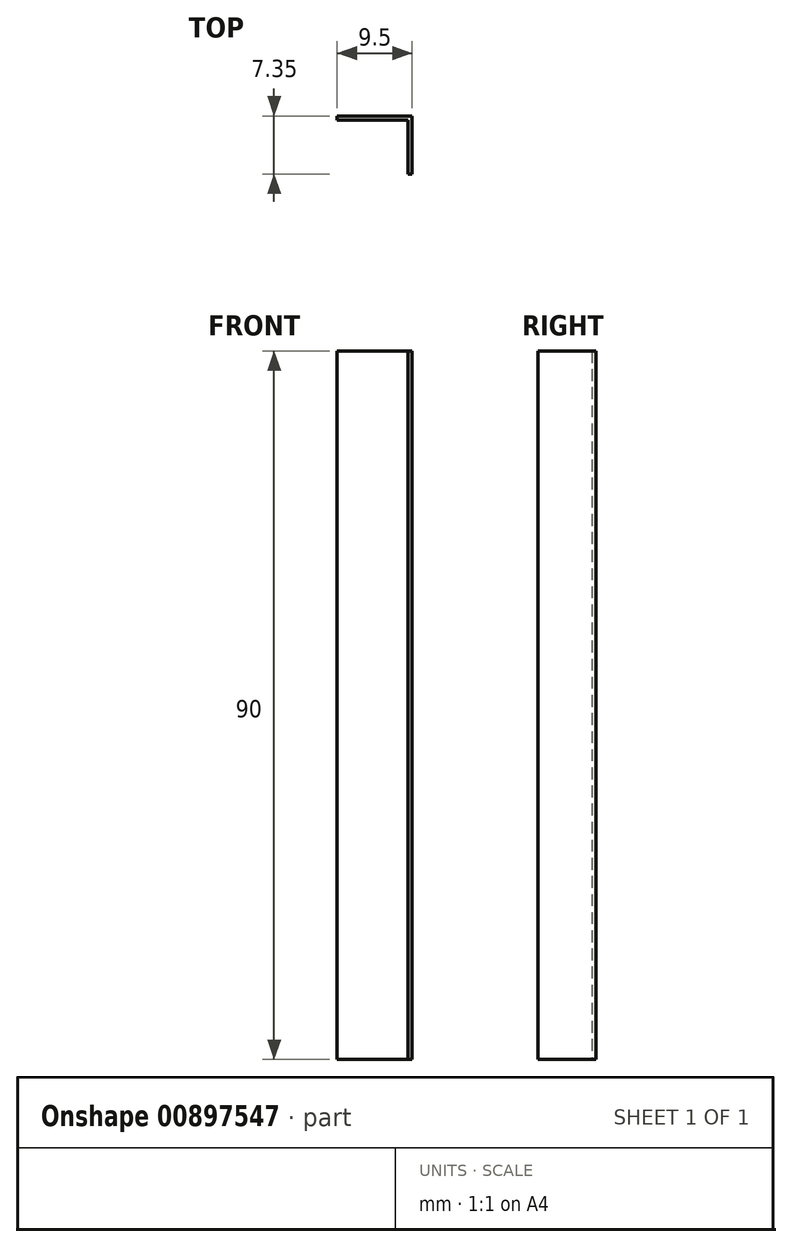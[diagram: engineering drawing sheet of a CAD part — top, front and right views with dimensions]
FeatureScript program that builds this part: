
annotation { "Feature Type Name" : "Feature", "Feature Type Description" : "" }
export const myFeature = defineFeature(function(context is Context, id is Id, definition is map)
    precondition{}
    {
        {
            var Q0;
            Q0=qCreatedBy(makeId("Top.planeOp"),FACE);
            var sketch = newSketch(context, id + "F0", { "sketchPlane" : qUnion([Q0])});
            skLineSegment(sketch, "E0", {"start": v(-48.18, 36.68) * mm, "end": v(-39.18, 36.68) * mm});
            skLineSegment(sketch, "E1", {"start": v(-39.18, 36.68) * mm, "end": v(-39.18, 36.18) * mm});
            skLineSegment(sketch, "E2.0", {"start": v(-38.68, 37.04) * mm, "end": v(-38.68, 36.18) * mm});
            skLineSegment(sketch, "E3.0", {"start": v(-48.18, 37.18) * mm, "end": v(-39.18, 37.18) * mm});
            skLineSegment(sketch, "E4", {"start": v(-39.18, 37.18) * mm, "end": v(-38.68, 37.18) * mm});
            skLineSegment(sketch, "E5", {"start": v(-38.68, 37.04) * mm, "end": v(-38.68, 37.18) * mm});
            skLineSegment(sketch, "E6", {"start": v(-48.18, 37.18) * mm, "end": v(-48.18, 36.68) * mm});
            skLineSegment(sketch, "E7", {"start": v(-39.18, 36.18) * mm, "end": v(-39.18, 29.83) * mm});
            skLineSegment(sketch, "E8", {"start": v(-39.18, 29.83) * mm, "end": v(-38.68, 29.83) * mm});
            skLineSegment(sketch, "E9", {"start": v(-38.68, 36.18) * mm, "end": v(-38.68, 29.83) * mm});
            skSolve(sketch);
        }
        {
            var Q0;
            Q0 = qSketchRegion(id + "F0", true);
            extrude(context, id + "F1", {"entities" : qUnion([Q0]), "depth" : 90 * mm, "offsetDistance" : 25 * mm});
        }
    });
